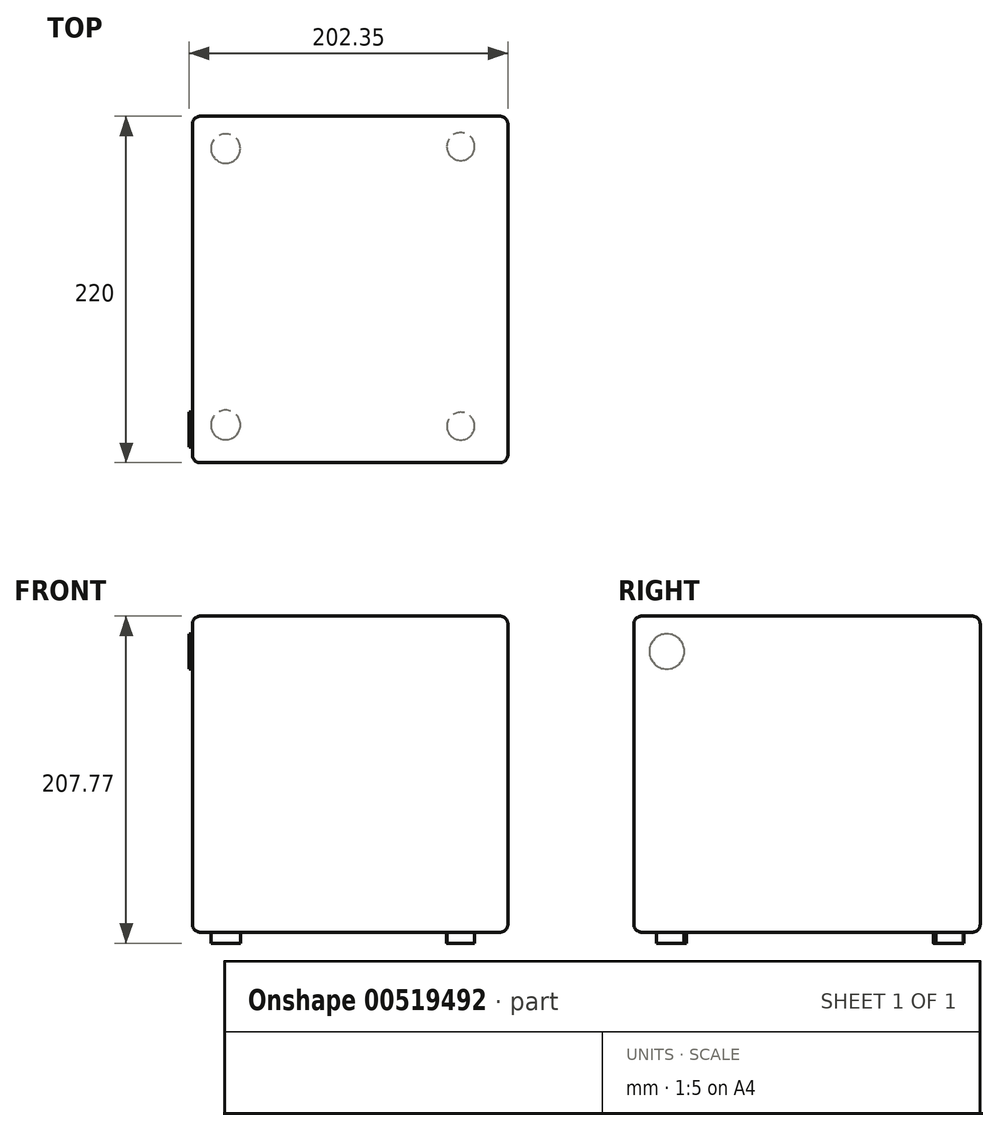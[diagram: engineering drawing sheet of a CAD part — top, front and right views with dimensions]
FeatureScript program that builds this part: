
annotation { "Feature Type Name" : "Feature", "Feature Type Description" : "" }
export const myFeature = defineFeature(function(context is Context, id is Id, definition is map)
    precondition{}
    {
        {
            var Q0;
            Q0=qCreatedBy(makeId("Front.planeOp"),FACE);
            var sketch = newSketch(context, id + "F0", { "sketchPlane" : qUnion([Q0])});
            skLineSegment(sketch, "E0.bottom", {"start": v(-64.65, 44.2) * mm, "end": v(135.7, 44.2) * mm});
            skLineSegment(sketch, "E0.top", {"start": v(-64.65, -156.58) * mm, "end": v(135.7, -156.58) * mm});
            skLineSegment(sketch, "E0.left", {"start": v(-64.65, 44.2) * mm, "end": v(-64.65, -156.58) * mm});
            skLineSegment(sketch, "E0.right", {"start": v(135.7, 44.2) * mm, "end": v(135.7, -156.58) * mm});
            skSolve(sketch);
        }
        {
            var Q0;
            Q0=makeQuery(id+"F0.imprint","IMPRINT",FACE,{"disambiguationData":[TD([[makeQuery(id+"F0.imprint","IMPRINT",EDGE,{"derivedFrom":sQuery(id+"F0.wireOp",EDGE,"E0.bottom")}),-1.0]])]});
            extrude(context, id + "F1", {"entities" : qUnion([Q0]), "depth" : 220 * mm, "offsetDistance" : 25 * mm});
        }
        {
            var Q0;
            Q0=makeQuery(id+"F1.opExtrude","CAP_FACE",FACE,{"disambiguationData":[OSD([sQuery(id+"F0.wireOp",EDGE,"E0.bottom"),sQuery(id+"F0.wireOp",EDGE,"E0.top"),sQuery(id+"F0.wireOp",EDGE,"E0.left"),sQuery(id+"F0.wireOp",EDGE,"E0.right")])],"isStart":false});
            var sketch = newSketch(context, id + "F2", { "sketchPlane" : qUnion([Q0])});
            skLineSegment(sketch, "E1.bottom", {"start": v(-19.44, 27.36) * mm, "end": v(87.12, 27.36) * mm});
            skLineSegment(sketch, "E1.top", {"start": v(-19.44, 14.61) * mm, "end": v(87.12, 14.61) * mm});
            skLineSegment(sketch, "E1.left", {"start": v(-19.44, 27.36) * mm, "end": v(-19.44, 14.61) * mm});
            skLineSegment(sketch, "E1.right", {"start": v(87.12, 27.36) * mm, "end": v(87.12, 14.61) * mm});
            skSolve(sketch);
        }
        {
            var Q0;
            Q0=makeQuery(id+"F2.imprint","IMPRINT",FACE,{"disambiguationData":[TD([[makeQuery(id+"F2.imprint","IMPRINT",EDGE,{"derivedFrom":sQuery(id+"F2.wireOp",EDGE,"E1.bottom")}),-1.0]])]});
            extrude(context, id + "F3", {"entities" : qUnion([Q0]), "operationType" : NewBodyOperationType.ADD, "depth" : -15 * mm, "offsetDistance" : 25 * mm});
        }
        {
            var Q0;
            Q0=makeQuery(id+"F1.opExtrude","CAP_EDGE",EDGE,{"disambiguationData":[OSD([sQuery(id+"F0.wireOp",EDGE,"E0.bottom")])],"isStart":false});
            fillet(context, id + "F4", {"entities" : qUnion([Q0]), "radius" : 5 * mm, "tangentPropagation" : true, "allowEdgeOverflow" : false});
        }
        {
            var Q0;
            Q0=makeQuery(id+"F4.opFillet","BLEND_EDGE",EDGE,{"blendedFrom":[makeQuery(id+"F1.opExtrude","CAP_EDGE",EDGE,{"disambiguationData":[OSD([sQuery(id+"F0.wireOp",EDGE,"E0.bottom")])],"isStart":false}),makeQuery(id+"F1.opExtrude","SWEPT_FACE",FACE,{"disambiguationData":[OSD([sQuery(id+"F0.wireOp",EDGE,"E0.right")])]})],"blendedInto":[makeQuery(id+"F1.opExtrude","SWEPT_FACE",FACE,{"disambiguationData":[OSD([sQuery(id+"F0.wireOp",EDGE,"E0.right")])]})]});
            fillet(context, id + "F5", {"entities" : qUnion([Q0]), "radius" : 5 * mm, "tangentPropagation" : true, "allowEdgeOverflow" : false});
        }
        {
            var Q0;
            Q0=makeQuery(id+"F4.opFillet","BLEND_EDGE",EDGE,{"blendedFrom":[makeQuery(id+"F1.opExtrude","CAP_EDGE",EDGE,{"disambiguationData":[OSD([sQuery(id+"F0.wireOp",EDGE,"E0.bottom")])],"isStart":false}),makeQuery(id+"F1.opExtrude","SWEPT_FACE",FACE,{"disambiguationData":[OSD([sQuery(id+"F0.wireOp",EDGE,"E0.left")])]})],"blendedInto":[makeQuery(id+"F1.opExtrude","SWEPT_FACE",FACE,{"disambiguationData":[OSD([sQuery(id+"F0.wireOp",EDGE,"E0.left")])]})]});
            fillet(context, id + "F6", {"entities" : qUnion([Q0]), "radius" : 5 * mm, "tangentPropagation" : true, "allowEdgeOverflow" : false});
        }
        {
            var Q0;
            Q0=makeQuery(id+"F1.opExtrude","SWEPT_FACE",FACE,{"disambiguationData":[OSD([sQuery(id+"F0.wireOp",EDGE,"E0.left")])]});
            var sketch = newSketch(context, id + "F7", { "sketchPlane" : qUnion([Q0])});
            skCircle(sketch, "E2", {"center": v(199.03, 21.76) * mm, "radius": 11.15 * mm});
            skLineSegment(sketch, "E3.bottom", {"start": v(215, -32.14) * mm, "end": v(169.72, -32.14) * mm});
            skLineSegment(sketch, "E3.top", {"start": v(215, -46.3) * mm, "end": v(169.72, -46.3) * mm});
            skLineSegment(sketch, "E3.left", {"start": v(215, -32.14) * mm, "end": v(215, -46.3) * mm});
            skLineSegment(sketch, "E3.right", {"start": v(169.72, -32.14) * mm, "end": v(169.72, -46.3) * mm});
            skLineSegment(sketch, "E4.bottom", {"start": v(215, -84.1) * mm, "end": v(169.42, -84.1) * mm});
            skLineSegment(sketch, "E4.top", {"start": v(215, -97.23) * mm, "end": v(169.42, -97.23) * mm});
            skLineSegment(sketch, "E4.left", {"start": v(215, -84.1) * mm, "end": v(215, -97.23) * mm});
            skLineSegment(sketch, "E4.right", {"start": v(169.42, -84.1) * mm, "end": v(169.42, -97.23) * mm});
            skSolve(sketch);
        }
        {
            var Q0;
            Q0=makeQuery(id+"F1.opExtrude","SWEPT_EDGE",EDGE,{"disambiguationData":[OSD([sQuery(id+"F0.wireOp",EDGE,"E0.top"),sQuery(id+"F0.wireOp",EDGE,"E0.right")])]});
            var Q1;
            Q1=makeQuery(id+"F1.opExtrude","CAP_EDGE",EDGE,{"disambiguationData":[OSD([sQuery(id+"F0.wireOp",EDGE,"E0.top")])],"isStart":false});
            var Q2;
            Q2=makeQuery(id+"F1.opExtrude","SWEPT_EDGE",EDGE,{"disambiguationData":[OSD([sQuery(id+"F0.wireOp",EDGE,"E0.top"),sQuery(id+"F0.wireOp",EDGE,"E0.left")])]});
            fillet(context, id + "F8", {"entities" : qUnion([Q0, Q1, Q2]), "radius" : 5 * mm, "tangentPropagation" : true, "allowEdgeOverflow" : false});
        }
        {
            var Q0;
            Q0=makeQuery(id+"F1.opExtrude","CAP_EDGE",EDGE,{"disambiguationData":[OSD([sQuery(id+"F0.wireOp",EDGE,"E0.top")])],"isStart":true});
            fillet(context, id + "F9", {"entities" : qUnion([Q0]), "radius" : 5 * mm, "tangentPropagation" : true, "allowEdgeOverflow" : false});
        }
        {
            var Q0;
            Q0=makeQuery(id+"F1.opExtrude","SWEPT_FACE",FACE,{"disambiguationData":[OSD([sQuery(id+"F0.wireOp",EDGE,"E0.top")])]});
            var sketch = newSketch(context, id + "F10", { "sketchPlane" : qUnion([Q0])});
            skCircle(sketch, "E5", {"center": v(26.57, 93.46) * mm, "radius": 72.18 * mm});
            skSolve(sketch);
        }
        {
            var Q0;
            Q0=makeQuery(id+"F1.opExtrude","SWEPT_FACE",FACE,{"disambiguationData":[OSD([sQuery(id+"F0.wireOp",EDGE,"E0.right")])]});
            var sketch = newSketch(context, id + "F11", { "sketchPlane" : qUnion([Q0])});
            skPoint(sketch, "E6.oppositeSnap0", {"position": v(-215, -56.2) * mm});
            skLineSegment(sketch, "E6.bottom", {"start": v(-215, -31.77) * mm, "end": v(-168.6, -31.77) * mm});
            skLineSegment(sketch, "E6.top", {"start": v(-215, -56.2) * mm, "end": v(-168.6, -56.2) * mm});
            skLineSegment(sketch, "E6.left", {"start": v(-215, -31.77) * mm, "end": v(-215, -56.2) * mm});
            skLineSegment(sketch, "E6.right", {"start": v(-168.6, -31.77) * mm, "end": v(-168.6, -56.2) * mm});
            skLineSegment(sketch, "E7.bottom", {"start": v(-215.9, -95.34) * mm, "end": v(-166.58, -95.34) * mm});
            skLineSegment(sketch, "E7.top", {"start": v(-215.9, -85.15) * mm, "end": v(-166.58, -85.15) * mm});
            skLineSegment(sketch, "E7.left", {"start": v(-215.9, -95.34) * mm, "end": v(-215.9, -85.15) * mm});
            skLineSegment(sketch, "E7.right", {"start": v(-166.58, -95.34) * mm, "end": v(-166.58, -85.15) * mm});
            skSolve(sketch);
        }
        {
            var Q0;
            Q0=makeQuery(id+"F2.imprint","IMPRINT",FACE,{"disambiguationData":[TD([[makeQuery(id+"F2.imprint","IMPRINT",EDGE,{"derivedFrom":sQuery(id+"F2.wireOp",EDGE,"E1.bottom")}),-1.0]])]});
            extrude(context, id + "F12", {"entities" : qUnion([Q0]), "operationType" : NewBodyOperationType.ADD, "oppositeDirection" : true, "depth" : 6.66 * mm, "offsetDistance" : 25 * mm});
        }
        {
            var Q0;
            Q0=makeQuery(id+"F10.imprint","IMPRINT",FACE,{"disambiguationData":[TD([[makeQuery(id+"F10.imprint","IMPRINT",EDGE,{"derivedFrom":sQuery(id+"F10.wireOp",EDGE,"E5")}),1.0]])]});
            var Q1;
            Q1 = qSketchRegion(id + "F10", true);
            var Q2;
            Q2=sQuery(id+"F2.wireOp",EDGE,"E1.right");
            var Q3;
            Q3=sQuery(id+"F2.wireOp",EDGE,"E1.left");
            var Q4;
            Q4=sQuery(id+"F2.wireOp",EDGE,"E1.top");
            var Q5;
            Q5=sQuery(id+"F2.wireOp",EDGE,"E1.bottom");
            extrude(context, id + "F13", {"entities" : qUnion([Q0, Q1]), "bodyType" : ToolBodyType.SURFACE, "surfaceEntities" : qUnion([Q2, Q3, Q4, Q5]), "oppositeDirection" : true, "depth" : 5 * mm, "offsetDistance" : 25 * mm});
        }
        {
            var Q0;
            Q0=makeQuery(id+"F1.opExtrude","SWEPT_FACE",FACE,{"disambiguationData":[OSD([sQuery(id+"F0.wireOp",EDGE,"E0.top")])]});
            var sketch = newSketch(context, id + "F14", { "sketchPlane" : qUnion([Q0])});
            skCircle(sketch, "E8", {"center": v(-43.51, 196.05) * mm, "radius": 9.35 * mm});
            skCircle(sketch, "E9", {"center": v(105.76, 196.83) * mm, "radius": 8.83 * mm});
            skCircle(sketch, "E10", {"center": v(-43.51, 20.49) * mm, "radius": 9.31 * mm});
            skCircle(sketch, "E11", {"center": v(105.76, 19.25) * mm, "radius": 8.87 * mm});
            skSolve(sketch);
        }
        {
            var Q0;
            Q0=makeQuery(id+"F14.imprint","IMPRINT",FACE,{"disambiguationData":[TD([[makeQuery(id+"F14.imprint","IMPRINT",EDGE,{"derivedFrom":sQuery(id+"F14.wireOp",EDGE,"E9")}),1.0]])]});
            var Q1;
            Q1=makeQuery(id+"F14.imprint","IMPRINT",FACE,{"disambiguationData":[TD([[makeQuery(id+"F14.imprint","IMPRINT",EDGE,{"derivedFrom":sQuery(id+"F14.wireOp",EDGE,"E11")}),1.0]])]});
            var Q2;
            Q2=makeQuery(id+"F14.imprint","IMPRINT",FACE,{"disambiguationData":[TD([[makeQuery(id+"F14.imprint","IMPRINT",EDGE,{"derivedFrom":sQuery(id+"F14.wireOp",EDGE,"E10")}),1.0]])]});
            var Q3;
            Q3=makeQuery(id+"F14.imprint","IMPRINT",FACE,{"disambiguationData":[TD([[makeQuery(id+"F14.imprint","IMPRINT",EDGE,{"derivedFrom":sQuery(id+"F14.wireOp",EDGE,"E8")}),1.0]])]});
            extrude(context, id + "F15", {"entities" : qUnion([Q0, Q1, Q2, Q3]), "operationType" : NewBodyOperationType.ADD, "depth" : 7 * mm, "offsetDistance" : 25 * mm});
        }
        {
            var Q0;
            {var subQ5=sQuery(id+"F11.wireOp",EDGE,"E6.bottom");Q0=makeQuery(id+"F11.imprint","IMPRINT",FACE,{"disambiguationData":[TD([[makeQuery(id+"F11.imprint","IMPRINT",EDGE,{"derivedFrom":subQ5}),1.0]])]});}
            var sketch = newSketch(context, id + "F16", { "sketchPlane" : qUnion([Q0])});
            skCircle(sketch, "E12", {"center": v(-199.47, 22.48) * mm, "radius": 7.3 * mm});
            skSolve(sketch);
        }
        {
            var Q0;
            Q0=sQuery(id+"F16.wireOp",EDGE,"E12");
            extrude(context, id + "F17", {"bodyType" : ToolBodyType.SURFACE, "surfaceEntities" : qUnion([Q0]), "depth" : 2 * mm, "offsetDistance" : 25 * mm});
        }
        {
            var Q0;
            Q0=makeQuery(id+"F7.imprint","IMPRINT",FACE,{"disambiguationData":[TD([[makeQuery(id+"F7.imprint","IMPRINT",EDGE,{"derivedFrom":sQuery(id+"F7.wireOp",EDGE,"E2")}),1.0]])]});
            extrude(context, id + "F18", {"entities" : qUnion([Q0]), "operationType" : NewBodyOperationType.ADD, "depth" : 2 * mm, "offsetDistance" : 25 * mm});
        }
    });
